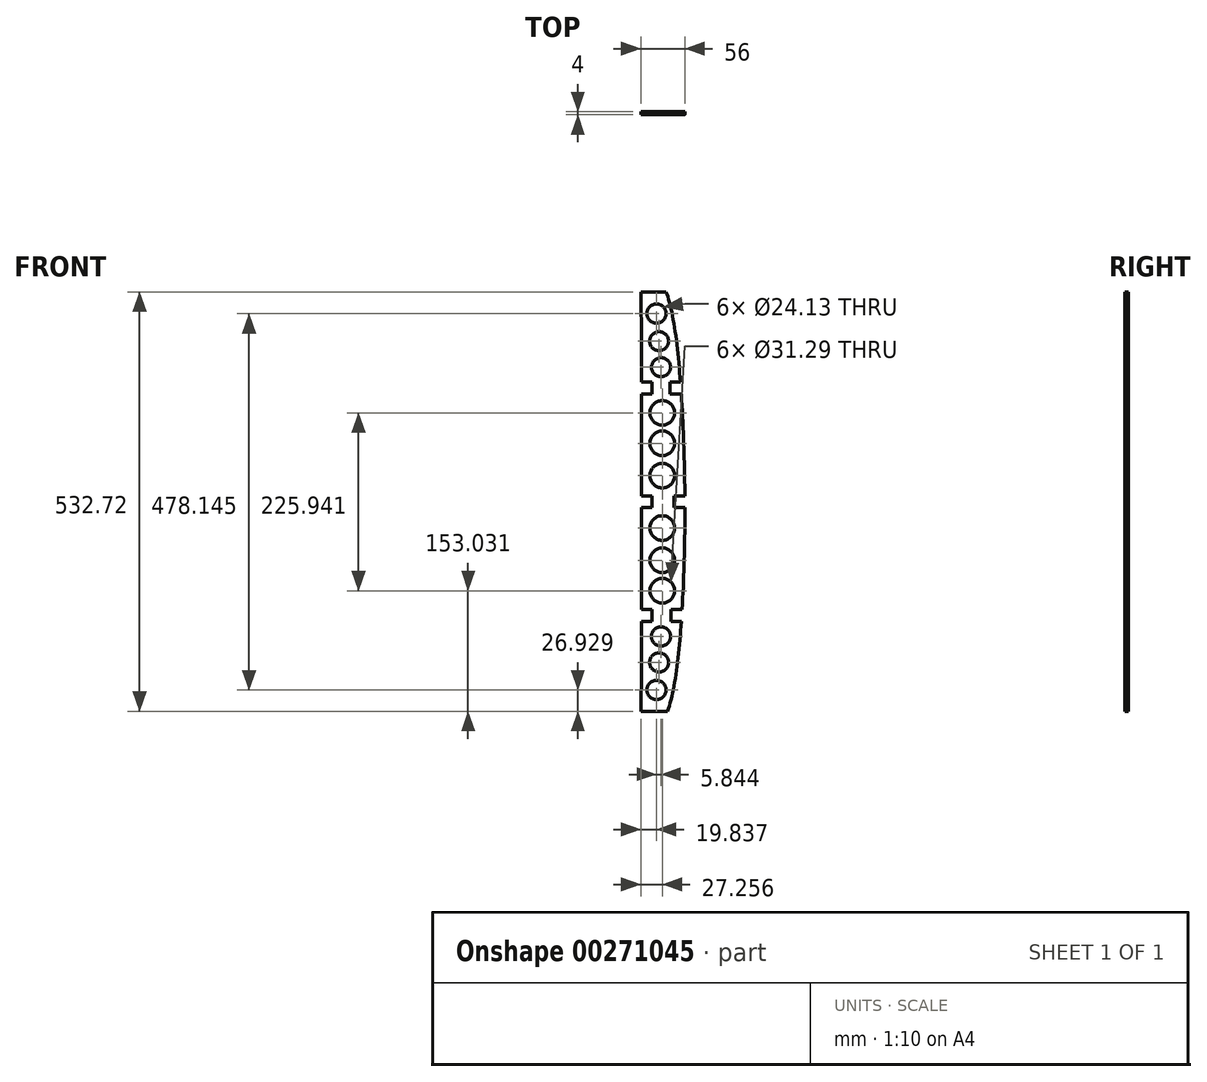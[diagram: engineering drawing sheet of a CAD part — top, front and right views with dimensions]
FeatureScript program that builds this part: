
annotation { "Feature Type Name" : "Feature", "Feature Type Description" : "" }
export const myFeature = defineFeature(function(context is Context, id is Id, definition is map)
    precondition{}
    {
        {
            var Q0;
            Q0=qCreatedBy(makeId("Front.planeOp"),FACE);
            var sketch = newSketch(context, id + "F0", { "sketchPlane" : qUnion([Q0])});
            skFitSpline(sketch, "E0", {"points": [v(587.2, 123.36) * mm, v(611.3, -143.36) * mm], "startDerivative": vector(70.48, -167.37) * mm, "endDerivative": vector(0.03, -5.04) * mm});
            skFitSpline(sketch, "E1.MirrorCS", {"points": [v(589.32, -409.36) * mm, v(611.3, -143.36) * mm], "startDerivative": vector(70.82, 193.82) * mm, "endDerivative": vector(0.18, 7.65) * mm});
            skLineSegment(sketch, "E2", {"start": v(587.2, 123.36) * mm, "end": v(563.2, 123.36) * mm});
            skLineSegment(sketch, "E3.MirrorCS", {"start": v(556.86, -409.36) * mm, "end": v(556.86, -409.36) * mm});
            skLineSegment(sketch, "E4", {"start": v(556.86, -409.36) * mm, "end": v(589.32, -409.36) * mm});
            skLineSegment(sketch, "E5", {"start": v(563.2, 123.36) * mm, "end": v(555.32, 123.36) * mm});
            skLineSegment(sketch, "E6", {"start": v(555.32, 123.36) * mm, "end": v(555.32, 102.64) * mm});
            skLineSegment(sketch, "E7", {"start": v(611.3, -143.36) * mm, "end": v(473.94, -143.36) * mm});
            skLineSegment(sketch, "E8", {"start": v(555.32, 123.36) * mm, "end": v(555.32, -409.36) * mm});
            skLineSegment(sketch, "E9", {"start": v(555.32, -409.36) * mm, "end": v(556.86, -409.36) * mm});
            skLineSegment(sketch, "E10", {"start": v(597.3, -143.36) * mm, "end": v(597.3, -135.86) * mm});
            skLineSegment(sketch, "E11", {"start": v(569.32, -143.36) * mm, "end": v(569.32, -135.86) * mm});
            skLineSegment(sketch, "E12.MirrorCS", {"start": v(597.3, -143.36) * mm, "end": v(597.3, -150.86) * mm});
            skLineSegment(sketch, "E13.MirrorCS", {"start": v(569.32, -143.36) * mm, "end": v(569.32, -150.86) * mm});
            skLineSegment(sketch, "E14", {"start": v(569.32, -135.86) * mm, "end": v(555.32, -135.86) * mm});
            skLineSegment(sketch, "E15", {"start": v(569.32, -150.86) * mm, "end": v(555.32, -150.86) * mm});
            skLineSegment(sketch, "E16", {"start": v(597.3, -150.86) * mm, "end": v(611.3, -150.86) * mm});
            skLineSegment(sketch, "E17", {"start": v(555.32, -143.36) * mm, "end": v(556.32, -143.36) * mm});
            skFitSpline(sketch, "E18", {"points": [v(555.32, 123.36) * mm, v(556.32, -143.36) * mm, v(555.32, -409.36) * mm], "startDerivative": vector(7.83, -361.23) * mm, "endDerivative": vector(-9.25, -335.41) * mm});
            skLineSegment(sketch, "E19", {"start": v(611.3, -150.86) * mm, "end": v(611.45, -150.86) * mm});
            skLineSegment(sketch, "E20", {"start": v(648.87, 1.14) * mm, "end": v(492.33, 1.14) * mm});
            skLineSegment(sketch, "E21", {"start": v(569.32, 8.64) * mm, "end": v(569.32, 1.14) * mm});
            skLineSegment(sketch, "E22.MirrorCS", {"start": v(569.32, -6.36) * mm, "end": v(569.32, 1.14) * mm});
            skLineSegment(sketch, "E23", {"start": v(569.32, 8.64) * mm, "end": v(555.32, 8.64) * mm});
            skLineSegment(sketch, "E24", {"start": v(569.32, -6.36) * mm, "end": v(555.32, -6.36) * mm});
            skLineSegment(sketch, "E25", {"start": v(592.66, -6.36) * mm, "end": v(606.66, -6.36) * mm});
            skLineSegment(sketch, "E26", {"start": v(592.66, -6.36) * mm, "end": v(592.66, 1.14) * mm});
            skLineSegment(sketch, "E27", {"start": v(592.66, 1.14) * mm, "end": v(592.66, 8.64) * mm});
            skLineSegment(sketch, "E28", {"start": v(592.66, 8.64) * mm, "end": v(605.62, 8.64) * mm});
            skLineSegment(sketch, "E29", {"start": v(597.3, -135.86) * mm, "end": v(611.26, -135.86) * mm});
            skCircle(sketch, "E30", {"center": v(582.58, -110.07) * mm, "radius": 15.64 * mm});
            skCircle(sketch, "E31", {"center": v(582.58, -69.05) * mm, "radius": 15.64 * mm});
            skCircle(sketch, "E32", {"center": v(582.58, -30.39) * mm, "radius": 15.64 * mm});
            skCircle(sketch, "E33", {"center": v(581, 27.68) * mm, "radius": 12.06 * mm});
            skCircle(sketch, "E34", {"center": v(578.5, 60.65) * mm, "radius": 12.06 * mm});
            skCircle(sketch, "E35", {"center": v(575.16, 95.71) * mm, "radius": 12.06 * mm});
            skCircle(sketch, "E36.MirrorC", {"center": v(582.58, -176.65) * mm, "radius": 15.64 * mm});
            skCircle(sketch, "E37.MirrorC", {"center": v(582.58, -217.66) * mm, "radius": 15.64 * mm});
            skCircle(sketch, "E38.MirrorC", {"center": v(582.58, -256.33) * mm, "radius": 15.64 * mm});
            skCircle(sketch, "E39.MirrorC", {"center": v(581, -314.4) * mm, "radius": 12.06 * mm});
            skCircle(sketch, "E40.MirrorC", {"center": v(578.5, -347.37) * mm, "radius": 12.06 * mm});
            skCircle(sketch, "E41.MirrorC", {"center": v(575.16, -382.43) * mm, "radius": 12.06 * mm});
            skLineSegment(sketch, "E42.MirrorCS", {"start": v(569.32, -280.36) * mm, "end": v(555.32, -280.36) * mm});
            skLineSegment(sketch, "E43.MirrorCS", {"start": v(569.32, -280.36) * mm, "end": v(569.32, -287.86) * mm});
            skLineSegment(sketch, "E44.MirrorCS", {"start": v(569.32, -295.36) * mm, "end": v(569.32, -287.86) * mm});
            skLineSegment(sketch, "E45", {"start": v(606.66, -280.36) * mm, "end": v(608.76, -280.36) * mm});
            skLineSegment(sketch, "E46", {"start": v(605.62, -295.36) * mm, "end": v(607.52, -295.36) * mm});
            skLineSegment(sketch, "E47", {"start": v(606.66, -280.36) * mm, "end": v(593.66, -280.36) * mm});
            skLineSegment(sketch, "E48", {"start": v(593.66, -280.36) * mm, "end": v(593.66, -295.36) * mm});
            skLineSegment(sketch, "E49", {"start": v(593.66, -295.36) * mm, "end": v(605.62, -295.36) * mm});
            skLineSegment(sketch, "E50", {"start": v(569.32, -295.36) * mm, "end": v(555.32, -295.36) * mm});
            skSolve(sketch);
        }
        {
            var Q0;
            {var subQ3=sQuery(id+"F0.wireOp",EDGE,"e4a9ef9c-881f-46ef-b2bc-2d1898208d58");Q0=makeQuery(id+"F0.imprint","IMPRINT",FACE,{"disambiguationData":[TD([[makeQuery(id+"F0.imprint","IMPRINT",EDGE,{"derivedFrom":subQ3}),-1.0]])]});}
            var Q1;
            Q1=makeQuery(id+"F0.imprint","IMPRINT",FACE,{"disambiguationData":[TD([[makeQuery(id+"F0.imprint","IMPRINT",EDGE,{"derivedFrom":sQuery(id+"F0.wireOp",EDGE,"4894cc72-ee94-4fed-bb0c-96aadf36fd790.MirrorCS")}),-1.0]])]});
            var Q2;
            Q2=makeQuery(id+"F0.imprint","IMPRINT",FACE,{"disambiguationData":[TD([[makeQuery(id+"F0.imprint","IMPRINT",EDGE,{"derivedFrom":sQuery(id+"F0.wireOp",EDGE,"166f034c-3e45-4ca4-938c-a2916eb385df.bottom")}),-1.0]])]});
            var Q3;
            Q3=makeQuery(id+"F0.imprint","IMPRINT",FACE,{"disambiguationData":[TD([[makeQuery(id+"F0.imprint","IMPRINT",EDGE,{"derivedFrom":sQuery(id+"F0.wireOp",EDGE,"ab3b4a69-6a9f-4f02-906b-2cae95dad881")}),-1.0]])]});
            var Q4;
            Q4=makeQuery(id+"F0.imprint","IMPRINT",FACE,{"disambiguationData":[TD([[makeQuery(id+"F0.imprint","IMPRINT",EDGE,{"derivedFrom":sQuery(id+"F0.wireOp",EDGE,"4894cc72-ee94-4fed-bb0c-96aadf36fd791.MirrorC")}),1.0]])]});
            var Q5;
            {var subQ12=sQuery(id+"F0.wireOp",EDGE,"E10");Q5=makeQuery(id+"F0.imprint","IMPRINT",FACE,{"disambiguationData":[TD([[makeQuery(id+"F0.imprint","IMPRINT",EDGE,{"derivedFrom":subQ12}),1.0]])]});}
            var Q6;
            {var subQ8=sQuery(id+"F0.wireOp",EDGE,"E2");Q6=makeQuery(id+"F0.imprint","IMPRINT",FACE,{"disambiguationData":[TD([[makeQuery(id+"F0.imprint","IMPRINT",EDGE,{"derivedFrom":subQ8}),1.0]])]});}
            var Q7;
            {var subQ17=sQuery(id+"F0.wireOp",EDGE,"E4");Q7=makeQuery(id+"F0.imprint","IMPRINT",FACE,{"disambiguationData":[TD([[makeQuery(id+"F0.imprint","IMPRINT",EDGE,{"derivedFrom":subQ17}),1.0]])]});}
            extrude(context, id + "F1", {"entities" : qUnion([Q0, Q1, Q2, Q3, Q4, Q5, Q6, Q7]), "depth" : 4 * mm});
        }
    });
